# Revit family: UNB_Specchio_Multiproduct_BIM_IT_T3364;T3365;T3366;T3367;T3368;T3369;T3371_NEW
name_source: partatom
category: Plumbing Fixtures
revit_build: Autodesk Revit 2017 (Build: 20160225_1515(x64)
units: mm (PartAtom-declared; Revit-internal decimal feet)

## family parameters
Cut with Voids When Loaded = No
Host = Face
Part Type = Normal
Room Calculation Point = No
Round Connector Dimension = Use Diameter
Shared = No

## types (7) — shared parameters
1200mmUnitOnly = Yes
Accessori = http://www.idealstandard.it
AltezzaNominale = 700 mm  [stored 2.29659 ft]
Autore = Ideal Standard
Brand = Ideal Standard
CodiceDiPrestazione = EN
Colore = specchio
Connessione = piombatura
Default Elevation = 1500 mm  [stored 4.92126 ft]
DescrizioneClassifcazioneUni2015 = Bathroom furniture
Finitura = specchio
Forma = rettangolare
Garanzia = garanzia del produttore
IfcEsportaCome = BATHROOM FURNITURE
InformazioniDiProdotto = http://www.idealstandard.it
InstruzioniInstallazione = http://www.idealstandard.it
LunghezzaNominale = 20 mm  [stored 0.0656168 ft]
Materiale = bicchiere
PartiDiRicambio = http://www.idealstandard.it
ProfonditàNominale = 20 mm  [stored 0.0656168 ft]
Revisione = 1
RiferimentoClassificazioneUni2015 = MIRRORS
Spazio = interno
Telefono = 800 652 290
TipoDiDato = Fisso
TipoEspotazioneIfc = IfcFurnitureType
TipologiaVaso = Altro
URL = http://www.idealstandard.it
UnitàDurata = anno
UnitàDurataGaranzia = anno
UnitàLineare = millimetro
UnitàMonetaria = €
UnitàSuperficie = millimetro
UnitàVolume = litro
Versione = 1
VersioneClassificazioneUni2015 = IfcFurnitureType
zero-valued in all types: Cost, CostoDiSostituzione

## per-type parameters (varying)
| type | Caratteristiche | CodiceABarre | Description | LarghezzaNominale | Model | ModelloDiRiferimento | Nome | NomeOggettoBim | NumeroDiModello | PesoNetto | Riferimento |
| T3364 - 400 x 700 mirror | SPECCHIO ECO 40X70 NO FRAME | 8014140447566 | SPECCHIO ECO 40X70 NO FRAME | 400 mm  [stored 1.31234 ft] | T3364BH | SPECCHIO ECO 40X70 NO FRAME | ISI_IdealStandard_Specchio_T3364 | ISI_IdealStandard_Specchio_T3364 | T3364BH | 4.06 Kg | T3364 |
| T3365 - 500 x 700 mirror | SPECCHIO ECO 50X70 NO FRAME | 8014140447573 | SPECCHIO ECO 50X70 NO FRAME | 500 mm  [stored 1.64042 ft] | T3365BH | SPECCHIO ECO 50X70 NO FRAME | ISI_IdealStandard_Specchio_T3365 | ISI_IdealStandard_Specchio_T3365 | T3365BH | 6.50 Kg | T3365 |
| T3366 - 600 x 700 mirror | SPECCHIO ECO 60X70 NO FRAME | 8014140447580 | SPECCHIO ECO 60X70 NO FRAME | 600 mm | T3366BH | SPECCHIO ECO 60X70 NO FRAME | ISI_IdealStandard_Specchio_T3366 | ISI_IdealStandard_Specchio_T3366 | T3366BH | 6.50 Kg | T3366 |
| T3367 - 700 x 700 mirror | SPECCHIO ECO 70X70 NO FRAME | 8014140447597 | SPECCHIO ECO 70X70 NO FRAME | 700 mm  [stored 2.29659 ft] | T3367BH | SPECCHIO ECO 70X70 NO FRAME | ISI_IdealStandard_Specchio_T3367 | ISI_IdealStandard_Specchio_T3367 | T3367BH | 7.00 Kg | T3367 |
| T3368 - 800 x 700 mirror | SPECCHIO ECO 80X70 NO FRAME | 8014140447603 | SPECCHIO ECO 80X70 NO FRAME | 800 mm  [stored 2.62467 ft] | T3368BH | SPECCHIO ECO 80X70 NO FRAME | ISI_IdealStandard_Specchio_T3368 | ISI_IdealStandard_Specchio_T3368 | T3368BH | 7.00 Kg | T3368 |
| T3369 - 1000 x 700 mirror | SPECCHIO ECO 100X70 NO FRAME | 8014140447610 | SPECCHIO ECO 100X70 NO FRAME | 1000 mm  [stored 3.28084 ft] | T3369BH | SPECCHIO ECO 100X70 NO FRAME | ISI_IdealStandard_Specchio_T3369 | ISI_IdealStandard_Specchio_T3369 | T3369BH | 7.50 Kg | T3369 |
| T3371 - 1200 x 700 mirror | SPECCHIO ECO 120X70 NO FRAME | 8014140447627 | SPECCHIO ECO 120X70 NO FRAME | 1200 mm  [stored 3.93701 ft] | T3371BH | SPECCHIO ECO 120X70 NO FRAME | ISI_IdealStandard_Specchio_T3371 | ISI_IdealStandard_Specchio_T3371 | T3371BH | 8.00 Kg | T3371 |

note: [stored X ft] marks values corroborated as IEEE doubles in the binary element streams (Revit-internal decimal feet)

## geometry (parser evidence)
native form markers: Sweep x1
no freeform markers — native parametric forms only
